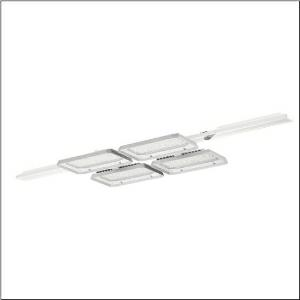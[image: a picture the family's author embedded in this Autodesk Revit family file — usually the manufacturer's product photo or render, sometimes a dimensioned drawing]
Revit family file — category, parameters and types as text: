
# Revit family: highbay_21_51hla2d24mlb
name_source: partatom
category: Lighting Fixtures
units: mm (PartAtom-declared; Revit-internal decimal feet)

## family parameters
Cut with Voids When Loaded = No
Host = Face
Light Source = No
Part Type = Normal
Room Calculation Point = No
Round Connector Dimension = Use Diameter
Shared = No

## types (1)
- --- (1 x LED, 27600 lm, 171.1 W, 4000K)
    Apparent Load = 171 VA
    CIE Flux Codes = 89 96 99 100 100
    Color Rendering = 80
    Color Temperature = 4000K
    Default Elevation = 1800 mm
    Description = Highbay 21, LED high bay luminaire, end cap, primary light control with lens, of PMMA, light emission: direct distribution, primary light characteristic: symmetric, installation type: recessed, for 2x 2 x LED rated luminous flux: 27.600 lm, light colour: 840, colour temperature: 4000K, control gear: ECG DALI, with system connector, mains connection: 230..240V, AC, 50/60Hz, rated input power: 171W, LED unit, of diecast aluminium, unplated, bead blasted, silver, length: 1.500 mm, width: 500 mm, height: 65mm, housing, of diecast aluminium, uncoated, bead blasted, silver, fixing on rail side, of aluminium, anodised, metallic grey, end cap, of PC, grey, protection rating (complete): IP64, insulation class (complete): insulation class I (protective earthing), certification: CE, protection symbol: D, impact resistance: IK08 with glass or PC cover, permissible ambient temperature for indoor applications: -35..+40°C, corresponds to IFS (International Featured Standards) requirements for safety and quality in the food industry, reducing of maximum allowable ambient temperature of 5°C with ceiling mounting, packaging unit: 1 piece
    Height = 105 mm
    Lamp = 1 x LED
    Lamp Light Flux = 27600 lm
    Lamp Power = 171.1 W
    Lamp count = 1
    Length = 1500 mm
    Luminous efficacy = 161 lm/W
    Manufacturer = Siteco
    ModVariant = No
    Model = 51HLA2D24MLB
    Mounting Place = Ceiling
    Mounting Type = Pendant
    Number of Poles = 1
    OnlyDefault = Yes
    Power Factor = 1
    Product Name = Highbay 21
    Product group = LED high bay luminaire
    ProductGroupID = 903
    Protection Class = Protection class I
    Protection Degree = IP 64
    RLX_Detail_Level = 1
    RlxData = <blob elided: 40797 chars, md5=d2ece67a>
    Socket = socket
    Standby Power = 0 W
    System Light Flux = 27600 lm
    System Power = 171 W
    Type Comments = factory setting: luminous flux: 100 % | dim-lin: 254 | 491 mA
    Type Image = l_1004707.jpg
    URL = http://relux.com
    VarID = @adj_135561
    Voltage = 0 V
    Weight = 0.00 kg
    Width = 500 mm

## geometry (parser evidence)
native form markers: Blend x4, Sweep x12
no freeform markers — native parametric forms only
